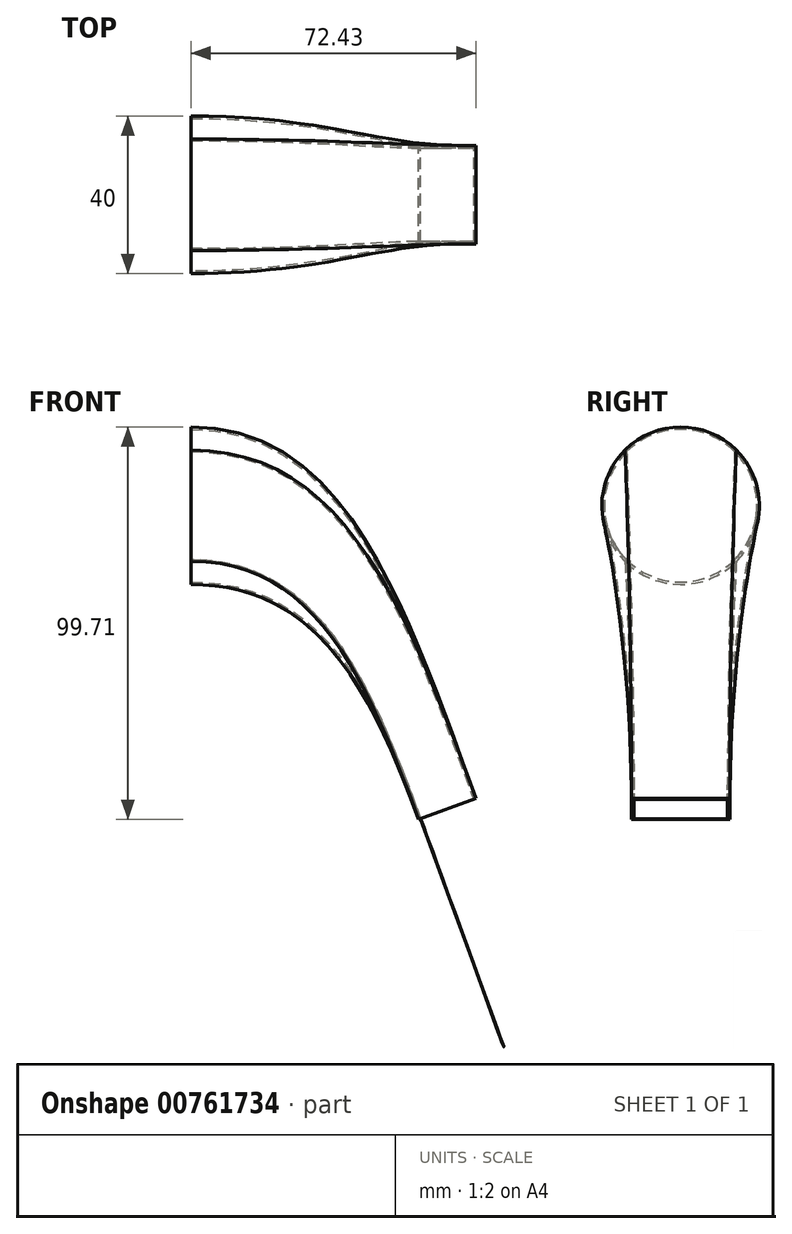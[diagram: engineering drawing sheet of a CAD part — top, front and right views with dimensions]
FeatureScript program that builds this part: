
annotation { "Feature Type Name" : "Feature", "Feature Type Description" : "" }
export const myFeature = defineFeature(function(context is Context, id is Id, definition is map)
    precondition{}
    {
        {
            var Q0;
            Q0=qCreatedBy(makeId("Right.planeOp"),FACE);
            var sketch = newSketch(context, id + "F0", { "sketchPlane" : qUnion([Q0])});
            skCircle(sketch, "E0", {"center": v(0, 100) * mm, "radius": 20 * mm});
            skLineSegment(sketch, "E1", {"start": v(0, 120) * mm, "end": v(0, 80) * mm, "construction": true});
            skLineSegment(sketch, "E2", {"start": v(20, 100) * mm, "end": v(-20, 100) * mm, "construction": true});
            skLineSegment(sketch, "E3", {"start": v(14.14, 114.14) * mm, "end": v(-14.14, 85.86) * mm, "construction": true});
            skLineSegment(sketch, "E4", {"start": v(14.4, 86.12) * mm, "end": v(-14.4, 113.88) * mm, "construction": true});
            skSolve(sketch);
        }
        {
            var Q0;
            Q0=qCreatedBy(makeId("Front.planeOp"),FACE);
            var sketch = newSketch(context, id + "F1", { "sketchPlane" : qUnion([Q0])});
            skLineSegment(sketch, "E5", {"start": v(57.29, 21.73) * mm, "end": v(71.9, 27.05) * mm});
            skLineSegment(sketch, "E6", {"start": v(71.9, 27.05) * mm, "end": v(72.43, 25.6) * mm});
            skLineSegment(sketch, "E7", {"start": v(72.43, 25.6) * mm, "end": v(57.81, 20.29) * mm});
            skLineSegment(sketch, "E8", {"start": v(57.81, 20.29) * mm, "end": v(57.29, 21.73) * mm});
            skSolve(sketch);
        }
        {
            var Q0;
            Q0=makeQuery(id+"F1.imprint","IMPRINT",FACE,{"disambiguationData":[TD([[makeQuery(id+"F1.imprint","IMPRINT",EDGE,{"derivedFrom":sQuery(id+"F1.wireOp",EDGE,"E5")}),-1.0]])]});
            extrude(context, id + "F2", {"entities" : qUnion([Q0]), "endBound" : BoundingType.SYMMETRIC, "depth" : 25 * mm, "offsetDistance" : 25 * mm});
        }
        {
            var Q1;
            Q1=makeQuery(id+"F0.imprint","IMPRINT",FACE,{"disambiguationData":[TD([[makeQuery(id+"F0.imprint","IMPRINT",EDGE,{"derivedFrom":sQuery(id+"F0.wireOp",EDGE,"E0")}),1.0]])]});
            var Q2;
            Q2=makeQuery(id+"F2.opExtrude","SWEPT_FACE",FACE,{"disambiguationData":[OSD([sQuery(id+"F1.wireOp",EDGE,"E5")])]});
            var Q3;
            Q3=sQuery(id+"F0.wireOp",VERTEX,"E3.start");
            var Q4;
            Q4=makeQuery(id+"F2.opExtrude","CAP_VERTEX",VERTEX,{"disambiguationData":[OSD([sQuery(id+"F1.wireOp",EDGE,"E5"),sQuery(id+"F1.wireOp",EDGE,"E6")])],"isStart":true});
            loft(context, id + "F3", {"operationType" : NewBodyOperationType.ADD, "startCondition" : LoftEndDerivativeType.NORMAL_TO_PROFILE, "startMagnitude" : 1.5, "endCondition" : LoftEndDerivativeType.NORMAL_TO_PROFILE, "endMagnitude" : 1.5, "sheetProfilesArray" : [{ "sheetProfileEntities" : qUnion([Q1]) }, { "sheetProfileEntities" : qUnion([Q2]) }], "matchConnections" : true, "connections" : [{ "connectionEntities" : qUnion([Q3, Q4]), "connectionEdgeQueries" : qUnion([]), "connectionEdgeParameters" : [] }]});
        }
        {
            var Q0;
            Q0=makeQuery(id+"F3.opLoft","CAP_FACE",FACE,{"disambiguationData":[OSD([makeQuery(id+"F0.imprint","IMPRINT",FACE,{"disambiguationData":[TD([[makeQuery(id+"F0.imprint","IMPRINT",EDGE,{"derivedFrom":sQuery(id+"F0.wireOp",EDGE,"E0")}),1.0]])]})])],"isStart":true});
            var Q1;
            Q1=makeQuery(id+"F2.opExtrude","SWEPT_FACE",FACE,{"disambiguationData":[OSD([sQuery(id+"F1.wireOp",EDGE,"E7")])]});
            shell(context, id + "F4", {"entities" : qUnion([Q0, Q1]), "thickness" : 0.6 * mm});
        }
    });
